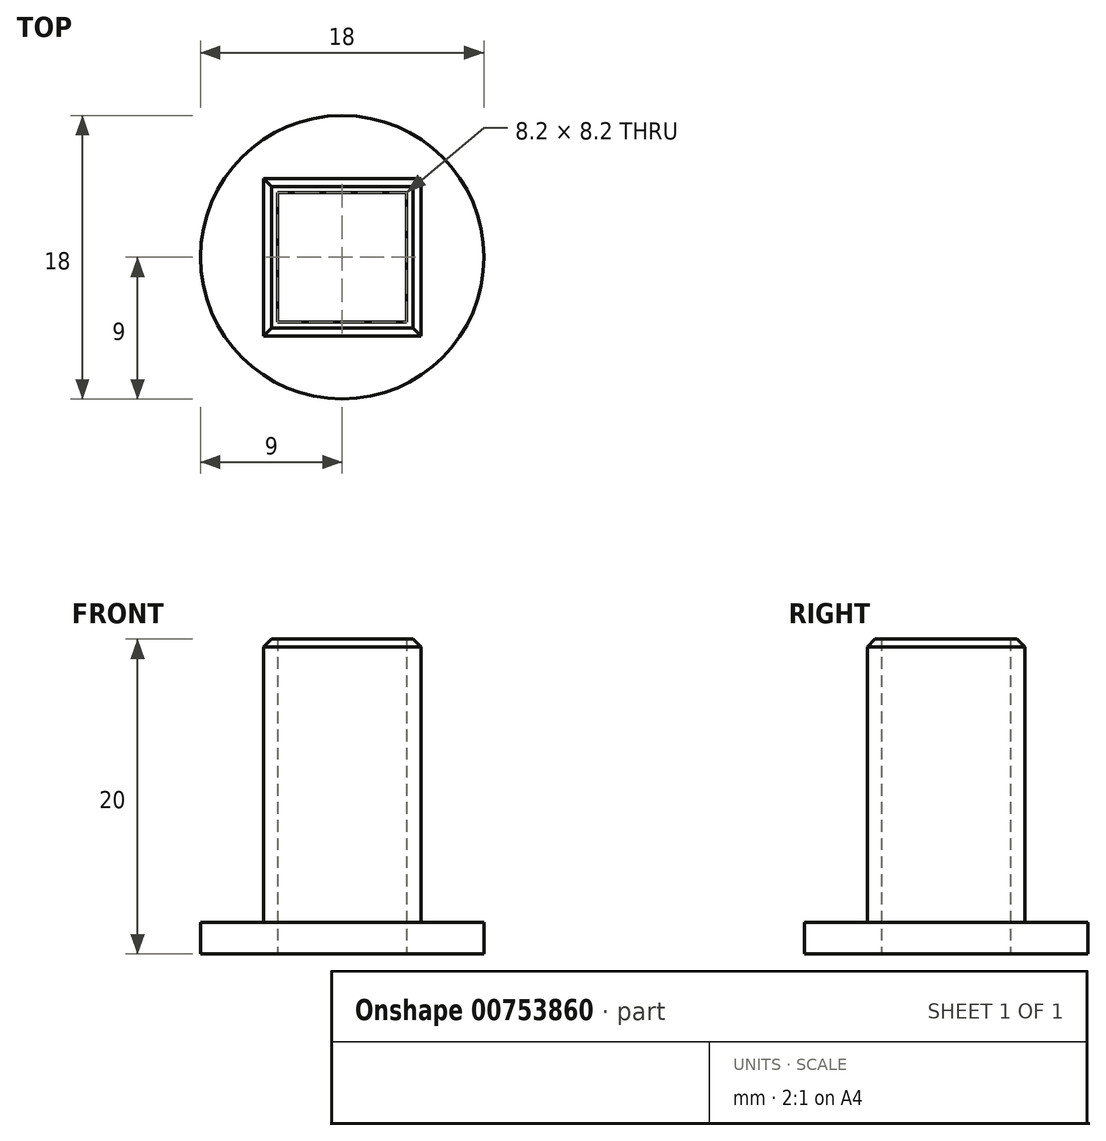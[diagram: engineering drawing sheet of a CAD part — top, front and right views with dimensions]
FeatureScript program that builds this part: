
annotation { "Feature Type Name" : "Feature", "Feature Type Description" : "" }
export const myFeature = defineFeature(function(context is Context, id is Id, definition is map)
    precondition{}
    {
        {
            var Q0;
            Q0=qCreatedBy(makeId("Top.planeOp"),FACE);
            var sketch = newSketch(context, id + "F0", { "sketchPlane" : qUnion([Q0])});
            skCircle(sketch, "E0", {"center": v(0, 0) * mm, "radius": 9 * mm});
            skLineSegment(sketch, "E1.bottom", {"start": v(4.1, 4.1) * mm, "end": v(-4.1, 4.1) * mm});
            skLineSegment(sketch, "E1.top", {"start": v(4.1, -4.1) * mm, "end": v(-4.1, -4.1) * mm});
            skLineSegment(sketch, "E1.left", {"start": v(4.1, 4.1) * mm, "end": v(4.1, -4.1) * mm});
            skLineSegment(sketch, "E1.right", {"start": v(-4.1, 4.1) * mm, "end": v(-4.1, -4.1) * mm});
            skLineSegment(sketch, "E2.bottom", {"start": v(5, 5) * mm, "end": v(-5, 5) * mm});
            skLineSegment(sketch, "E2.top", {"start": v(5, -5) * mm, "end": v(-5, -5) * mm});
            skLineSegment(sketch, "E2.left", {"start": v(5, 5) * mm, "end": v(5, -5) * mm});
            skLineSegment(sketch, "E2.right", {"start": v(-5, 5) * mm, "end": v(-5, -5) * mm});
            skSolve(sketch);
        }
        {
            var Q0;
            Q0=makeQuery(id+"F0.imprint","IMPRINT",FACE,{"disambiguationData":[TD([[makeQuery(id+"F0.imprint","IMPRINT",EDGE,{"derivedFrom":sQuery(id+"F0.wireOp",EDGE,"E0")}),1.0]])]});
            var Q1;
            Q1=makeQuery(id+"F0.imprint","IMPRINT",FACE,{"disambiguationData":[TD([[makeQuery(id+"F0.imprint","IMPRINT",EDGE,{"derivedFrom":sQuery(id+"F0.wireOp",EDGE,"E1.bottom")}),-1.0]])]});
            extrude(context, id + "F1", {"entities" : qUnion([Q0, Q1]), "depth" : 2 * mm, "offsetDistance" : 25 * mm});
        }
        {
            var Q0;
            Q0=makeQuery(id+"F0.imprint","IMPRINT",FACE,{"disambiguationData":[TD([[makeQuery(id+"F0.imprint","IMPRINT",EDGE,{"derivedFrom":sQuery(id+"F0.wireOp",EDGE,"E1.bottom")}),-1.0]])]});
            extrude(context, id + "F2", {"entities" : qUnion([Q0]), "operationType" : NewBodyOperationType.ADD, "depth" : 20 * mm, "offsetDistance" : 25 * mm});
        }
        {
            var Q0;
            Q0=makeQuery(id+"F2.opExtrude","CAP_EDGE",EDGE,{"disambiguationData":[OSD([sQuery(id+"F0.wireOp",EDGE,"E2.top")])],"isStart":false});
            var Q1;
            Q1=makeQuery(id+"F2.opExtrude","CAP_EDGE",EDGE,{"disambiguationData":[OSD([sQuery(id+"F0.wireOp",EDGE,"E2.left")])],"isStart":false});
            var Q2;
            Q2=makeQuery(id+"F2.opExtrude","CAP_EDGE",EDGE,{"disambiguationData":[OSD([sQuery(id+"F0.wireOp",EDGE,"E2.bottom")])],"isStart":false});
            var Q3;
            Q3=makeQuery(id+"F2.opExtrude","CAP_EDGE",EDGE,{"disambiguationData":[OSD([sQuery(id+"F0.wireOp",EDGE,"E2.right")])],"isStart":false});
            chamfer(context, id + "F3", {"entities" : qUnion([Q0, Q1, Q2, Q3]), "width" : 0.5 * mm, "tangentPropagation" : true});
        }
    });
